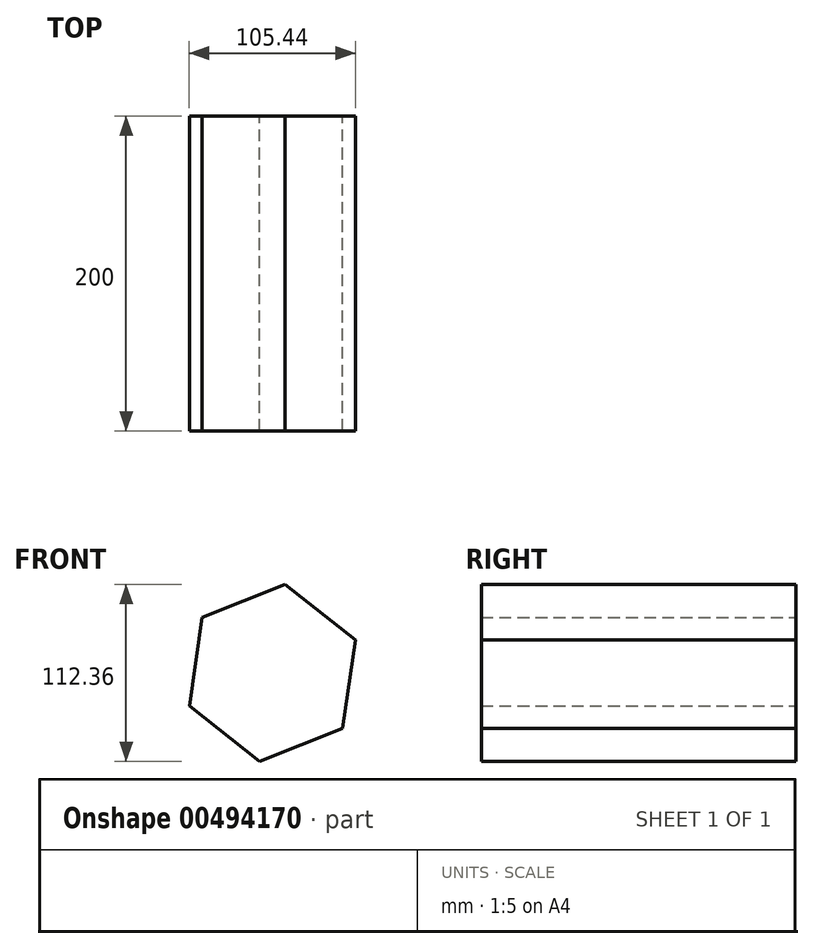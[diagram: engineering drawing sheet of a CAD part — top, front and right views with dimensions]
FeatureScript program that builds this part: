
annotation { "Feature Type Name" : "Feature", "Feature Type Description" : "" }
export const myFeature = defineFeature(function(context is Context, id is Id, definition is map)
    precondition{}
    {
        {
            var Q0;
            Q0=qCreatedBy(makeId("Front.planeOp"),FACE);
            var sketch = newSketch(context, id + "F0", { "sketchPlane" : qUnion([Q0])});
            skCircle(sketch, "E0.cCircle", {"center": v(0, 0) * mm, "radius": 56.77 * mm, "construction": true});
            skLineSegment(sketch, "E0.0", {"start": v(-44.6, 35.12) * mm, "end": v(8.12, 56.18) * mm});
            skLineSegment(sketch, "E0.1", {"start": v(8.12, 56.18) * mm, "end": v(52.72, 21.06) * mm});
            skLineSegment(sketch, "E0.2", {"start": v(52.72, 21.06) * mm, "end": v(44.6, -35.12) * mm});
            skLineSegment(sketch, "E0.3", {"start": v(44.6, -35.12) * mm, "end": v(-8.12, -56.18) * mm});
            skLineSegment(sketch, "E0.4", {"start": v(-8.12, -56.18) * mm, "end": v(-52.72, -21.06) * mm});
            skLineSegment(sketch, "E0.5", {"start": v(-52.72, -21.06) * mm, "end": v(-44.6, 35.12) * mm});
            skSolve(sketch);
        }
        {
            var Q0;
            Q0=makeQuery(id+"F0.imprint","IMPRINT",FACE,{"disambiguationData":[TD([[makeQuery(id+"F0.imprint","IMPRINT",EDGE,{"derivedFrom":sQuery(id+"F0.wireOp",EDGE,"E0.0")}),-1.0]])]});
            extrude(context, id + "F1", {"entities" : qUnion([Q0]), "endBound" : BoundingType.SYMMETRIC, "depth" : 200 * mm});
        }
    });
